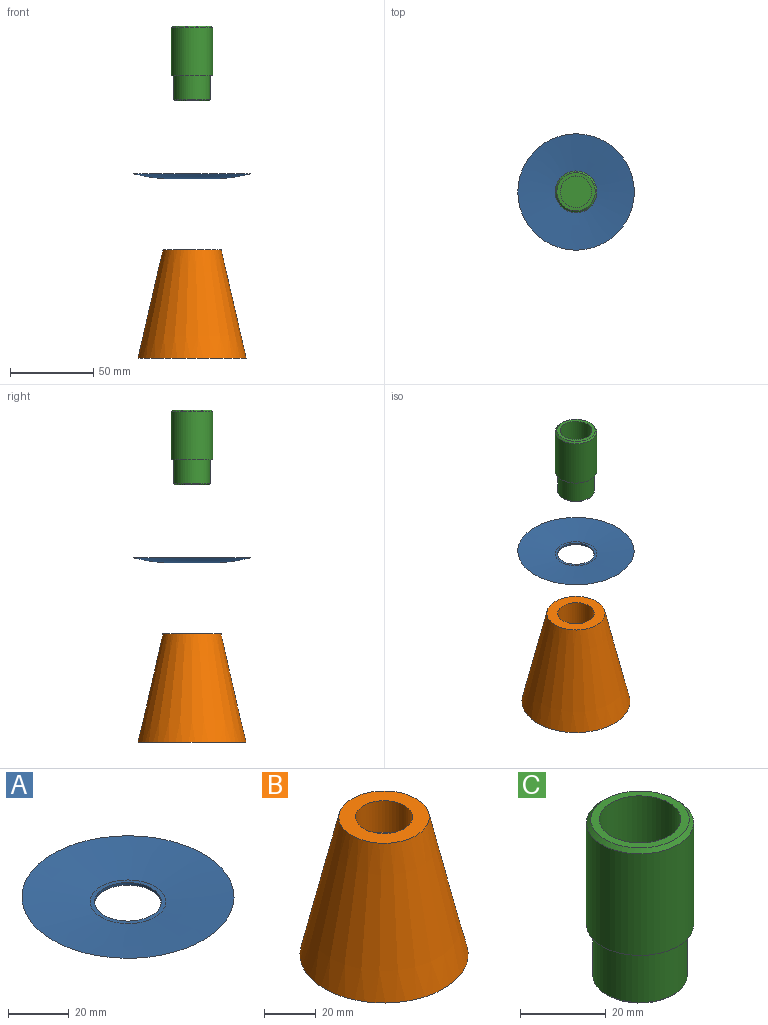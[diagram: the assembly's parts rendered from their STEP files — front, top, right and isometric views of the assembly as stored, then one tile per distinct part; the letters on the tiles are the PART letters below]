
ASSEMBLY  parts=3 mates=2
PART A: 5 faces, bbox 70x70x3 mm
  f0: plane 25x25mm, normal (0,0,-1), area 110.7mm2, adj f3,f4
  f1: plane 25x25mm, normal (0,0,1), area 110.7mm2, adj f2,f4
  f2: cone r=35mm half-angle=85.1deg, axis (0,0,1), area 3370.1mm2, adj f1,f3
  f3: torus R=12.5mm, axis (0,0,-1), area 3406.7mm2, adj f0,f2
  f4: cylinder r=11mm len=22mm, axis (0,0,1), area 73.1mm2, adj f0,f1
PART B: 7 faces, bbox 65x65x65 mm
  f0: plane 35x35mm, normal (0,0,1), area 582mm2, adj f1,f3
  f1: cone r=17.5mm half-angle=13deg, axis (0,0,-1), area 10478.5mm2, adj f0,f2
  f2: plane 65x65mm, normal (0,0,-1), area 3318.3mm2, adj f1
  f3: cylinder r=11mm len=22mm, axis (0,0,1), area 1036.7mm2, adj f0,f4
  f4: plane 22x22mm, normal (0,0,1), area 301.6mm2, adj f3,f5
  f5: cylinder r=5mm len=15mm, axis (0,0,1), area 471.2mm2, adj f4,f6
  f6: plane 10x10mm, normal (0,0,1), area 78.5mm2, adj f5
PART C: 9 faces, bbox 25x25x45 mm
  f0: cylinder r=12.5mm len=29mm, axis (0,0,-1), area 2277.7mm2, adj f2,f5
  f1: plane 23x23mm, normal (0,0,1), area 131.9mm2, adj f5,f7
  f2: plane 25x25mm, normal (0,0,-1), area 110.7mm2, adj f0,f3
  f3: cylinder r=11mm len=22mm, axis (0,0,1), area 1002.2mm2, adj f2,f6
  f4: plane 21x21mm, normal (0,0,-1), area 346.4mm2, adj f6
  f5: cone r=11.5mm half-angle=45deg, axis (0,0,-1), area 106.6mm2, adj f0,f1
  f6: cone r=10.5mm half-angle=45deg, axis (0,0,1), area 47.8mm2, adj f3,f4
  f7: cylinder r=9.5mm len=44.53mm, axis (0,0,1), area 2658mm2, adj f1,f8
  f8: plane 19x19mm, normal (0,0,1), area 283.5mm2, adj f7
PLACE A t=(-0.02,-0.34,74.8)mm
PLACE B t=(-0.02,-0.34,-7.13)mm fixed
PLACE C t=(-0.02,-0.34,136.74)mm
MATE slider A.f4 <-> B.f1  axis (0,0,1) through (-0.02,-0.34,75.86)mm
MATE slider C.f0 <-> A.f4  axis (0,0,-1) through (-0.02,-0.34,151.24)mm
